# Revit family: DBLTD_TheSenatorGroup_OfficeChairs_Uku
name_source: partatom
category: Furniture
units: mm (PartAtom-declared; Revit-internal decimal feet)

## family parameters
Always vertical = Yes
Cut with Voids When Loaded = No
OmniClass Number = 23.40.20.00
OmniClass Title = General Furniture and Specialties
Render Appearance Source = Family Geometry
Room Calculation Point = No
Shared = Yes
Work Plane-Based = No

## types (3) — shared parameters
Assembly Code = E2020200
AssetType = Movable
Category = Pr_40_50_12_57 Office chairs
Color = Wood: Solid Oak with Clear Finish or Black (Stained). Upholstery: Various
Constituents = Seat and Frame
DurationUnit = years
ExpectedLife = 5
Finish = Wood: Solid Oak with Clear Finish or Black (Stained). Upholstery: Various
FrameMaterial = DBLTD_TheSenatorGroup_Wood_Oak
Keynote = Pr_40_50_12_57 Office chairs
Manufacturer = The Senator Group
ManufacturerName = The Senator Group
ManufacturerURL = https://www.allermuir.com
Material = Wood: Solid Oak with Clear Finish or Black (Stained). Upholstery: Various
Name = Chair
ProductInformation = https://www.allermuir.com
SeatingHeight = 440 mm  [stored 1.44357 ft]
Shape = Rectangular
URL = https://www.thesenatorgroup.com
Uniclass2015Code = Pr_40_50_12_57
Uniclass2015Title = Office chairs
Uniclass2015Version = Products v1.15
Version = 1
WarrantyDescription = The Senator Group warrants that its manufactured products are free from manufacturing defects - in materials or workmanship - for a period of five (5) years.
WarrantyDurationLabor = 5
WarrantyDurationParts = 5
WarrantyDurationUnit = years
WarrantyGuarantorLabor = https://www.thesenatorgroup.com
WarrantyGuarantorParts = https://www.thesenatorgroup.com
zero-valued in all types: Cost, Default Elevation

## per-type parameters (varying)
| type | FrameType | Model | ModelNumber | NominalDepth | NominalHeight | NominalWidth | SeatType | Size |
| Mid Back Lounge Chair | Nested_DBLTD_TheSenatorGroup_OfficeChairs_Uku_SeatFrame | UKU301 | UKU301 | 860 mm | 1040 mm  [stored 3.41207 ft] | 770 mm  [stored 2.52625 ft] | Nested_DBLTD_TheSenatorGroup_OfficeChairs_Uku_HighBack | 1040 x 770 x 860 mm |
| Low Back Lounge Chair | Nested_DBLTD_TheSenatorGroup_OfficeChairs_Uku_SeatFrame | UKU201 | UKU201 | 800 mm  [stored 2.62467 ft] | 840 mm  [stored 2.75591 ft] | 770 mm  [stored 2.52625 ft] | Nested_DBLTD_TheSenatorGroup_OfficeChairs_Uku_LowBack | 840 x 770 x 800 mm |
| Ottoman | Nested_DBLTD_TheSenatorGroup_OfficeChairs_Uku_OttomanFrame | UKU101 | UKU101 | 490 mm  [stored 1.60761 ft] | 390 mm  [stored 1.27953 ft] | 585 mm  [stored 1.91929 ft] | Nested_DBLTD_TheSenatorGroup_OfficeChairs_Uku_Ottoman | 390 x 585 x 490 mm |

note: column(s) folded — value = type name in every type: Description, ModelReference, Type Comments

note: [stored X ft] marks values corroborated as IEEE doubles in the binary element streams (Revit-internal decimal feet)

## geometry (parser evidence)
native form markers: Sweep x18
no freeform markers — native parametric forms only
